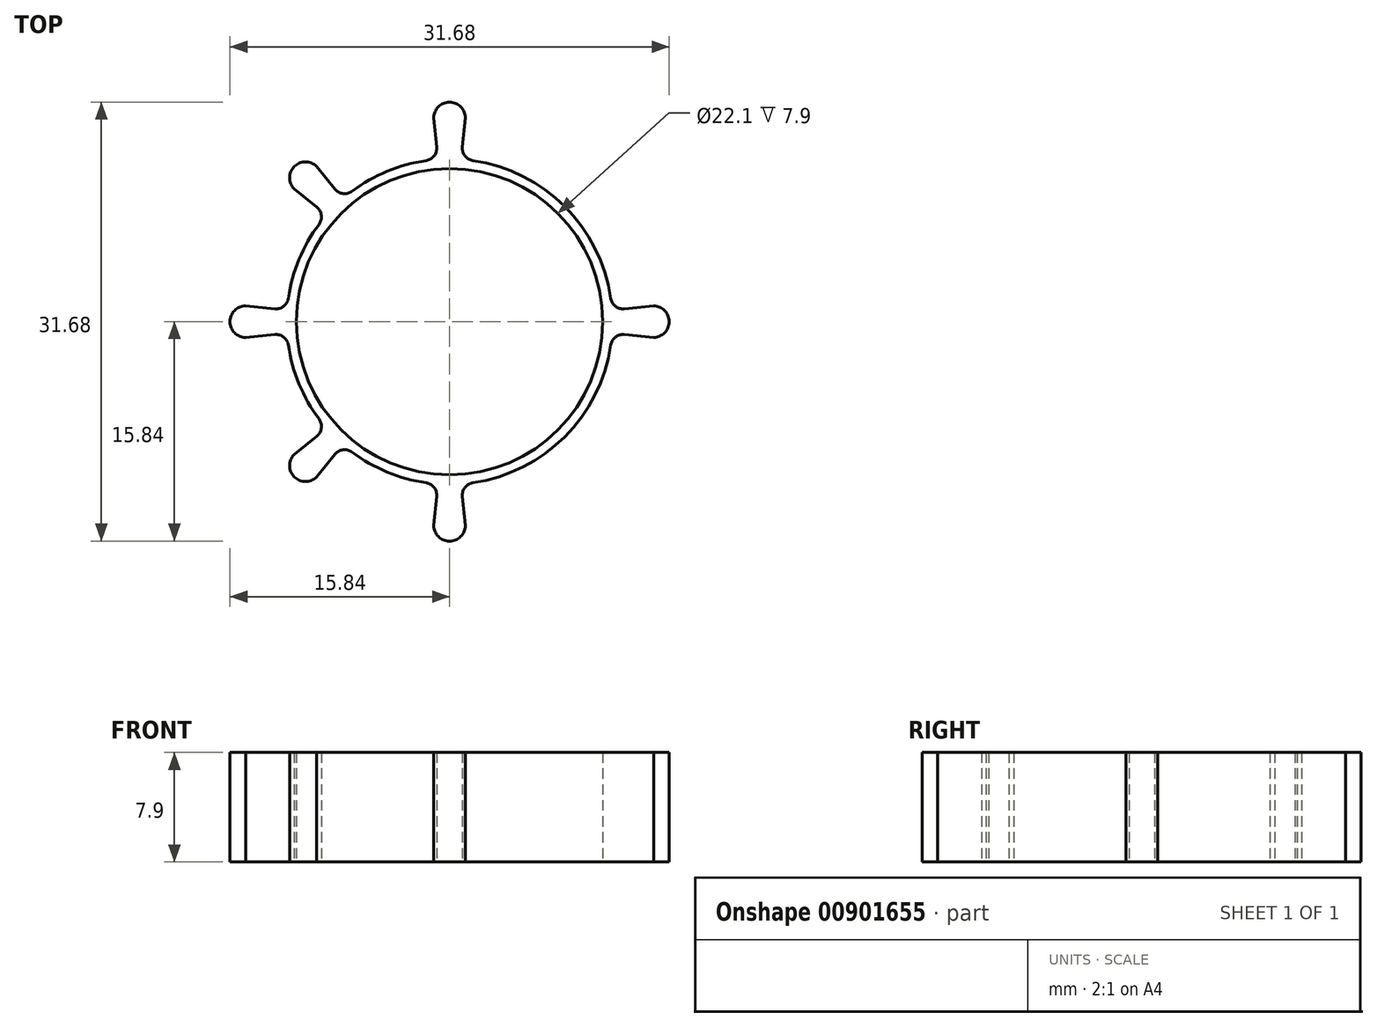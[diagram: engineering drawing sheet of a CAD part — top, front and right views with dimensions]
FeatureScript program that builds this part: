
annotation { "Feature Type Name" : "Feature", "Feature Type Description" : "" }
export const myFeature = defineFeature(function(context is Context, id is Id, definition is map)
    precondition{}
    {
        {
            var Q0;
            Q0=qCreatedBy(makeId("Top.planeOp"),FACE);
            var sketch = newSketch(context, id + "F0", { "sketchPlane" : qUnion([Q0])});
            skCircle(sketch, "E0", {"center": v(0, 0) * mm, "radius": 11.05 * mm});
            skCircle(sketch, "E1", {"center": v(0, 0) * mm, "radius": 11.75 * mm});
            skCircle(sketch, "E2", {"center": v(0, 0) * mm, "radius": 16 * mm, "construction": true});
            skLineSegment(sketch, "E3", {"start": v(-0.84, 11.72) * mm, "end": v(-1.15, 14.71) * mm});
            skLineSegment(sketch, "E4.MirrorCS", {"start": v(0.84, 11.72) * mm, "end": v(1.15, 14.71) * mm});
            skArc(sketch, "E5", {"start": v(1.15, 14.71) * mm, "mid": v(0, 15.84) * mm, "end": v(-1.15, 14.71) * mm});
            skLineSegment(sketch, "E6.MirrorCS", {"start": v(0.84, -11.72) * mm, "end": v(1.15, -14.71) * mm});
            skLineSegment(sketch, "E7.MirrorCS", {"start": v(-0.84, -11.72) * mm, "end": v(-1.15, -14.71) * mm});
            skArc(sketch, "E8.MirrorCS", {"start": v(1.15, -14.71) * mm, "mid": v(0, -15.84) * mm, "end": v(-1.15, -14.71) * mm});
            skLineSegment(sketch, "E9", {"start": v(0, 0) * mm, "end": v(-14.12, -14.12) * mm, "construction": true});
            skLineSegment(sketch, "E10", {"start": v(0, 0) * mm, "end": v(12.5, 12.5) * mm, "construction": true});
            skArc(sketch, "E11.MirrorCS", {"start": v(14.71, -1.15) * mm, "mid": v(15.84, 0) * mm, "end": v(14.71, 1.15) * mm});
            skLineSegment(sketch, "E12.MirrorCS", {"start": v(11.72, 0.84) * mm, "end": v(14.71, 1.15) * mm});
            skLineSegment(sketch, "E13.MirrorCS", {"start": v(11.72, -0.84) * mm, "end": v(14.71, -1.15) * mm});
            skLineSegment(sketch, "E14.MirrorCS", {"start": v(-11.72, 0.84) * mm, "end": v(-14.71, 1.15) * mm});
            skLineSegment(sketch, "E15.MirrorCS", {"start": v(-11.72, -0.84) * mm, "end": v(-14.71, -1.15) * mm});
            skArc(sketch, "E16.MirrorCS", {"start": v(-14.71, -1.15) * mm, "mid": v(-15.84, 0) * mm, "end": v(-14.71, 1.15) * mm});
            skLineSegment(sketch, "E17", {"start": v(0, 0) * mm, "end": v(18.87, 7.82) * mm, "construction": true});
            skLineSegment(sketch, "E18", {"start": v(0, 0) * mm, "end": v(-19, -7.87) * mm, "construction": true});
            skArc(sketch, "E19.MirrorCS", {"start": v(9.6, 11.22) * mm, "mid": v(11.2, 11.2) * mm, "end": v(11.22, 9.6) * mm});
            skLineSegment(sketch, "E20.MirrorCS", {"start": v(8.88, 7.7) * mm, "end": v(11.22, 9.6) * mm});
            skLineSegment(sketch, "E21.MirrorCS", {"start": v(7.7, 8.88) * mm, "end": v(9.6, 11.22) * mm});
            skLineSegment(sketch, "E22.MirrorCS", {"start": v(-8.88, -7.7) * mm, "end": v(-11.22, -9.6) * mm});
            skLineSegment(sketch, "E23.MirrorCS", {"start": v(-7.7, -8.88) * mm, "end": v(-9.6, -11.22) * mm});
            skArc(sketch, "E24.MirrorCS", {"start": v(-11.22, -9.6) * mm, "mid": v(-11.2, -11.2) * mm, "end": v(-9.6, -11.22) * mm});
            skLineSegment(sketch, "E25", {"start": v(0, 0) * mm, "end": v(-24.8, 10.27) * mm, "construction": true});
            skLineSegment(sketch, "E26", {"start": v(0, 0) * mm, "end": v(24.1, -9.98) * mm, "construction": true});
            skArc(sketch, "E27.MirrorCS", {"start": v(11.22, -9.6) * mm, "mid": v(11.2, -11.2) * mm, "end": v(9.6, -11.22) * mm});
            skLineSegment(sketch, "E28.MirrorCS", {"start": v(7.7, -8.88) * mm, "end": v(9.6, -11.22) * mm});
            skLineSegment(sketch, "E29.MirrorCS", {"start": v(8.88, -7.7) * mm, "end": v(11.22, -9.6) * mm});
            skLineSegment(sketch, "E30.MirrorCS", {"start": v(-7.7, 8.88) * mm, "end": v(-9.6, 11.22) * mm});
            skLineSegment(sketch, "E31.MirrorCS", {"start": v(-8.88, 7.7) * mm, "end": v(-11.22, 9.6) * mm});
            skArc(sketch, "E32.MirrorCS", {"start": v(-9.6, 11.22) * mm, "mid": v(-11.2, 11.2) * mm, "end": v(-11.22, 9.6) * mm});
            skSolve(sketch);
        }
        {
            var Q0;
            {var subQ0=sQuery(id+"F0.wireOp",EDGE,"E30.MirrorCS");Q0=makeQuery(id+"F0.imprint","IMPRINT",FACE,{"disambiguationData":[TD([[makeQuery(id+"F0.imprint","IMPRINT",EDGE,{"derivedFrom":subQ0}),1.0]])]});}
            var Q1;
            Q1=makeQuery(id+"F0.imprint","IMPRINT",FACE,{"disambiguationData":[TD([[makeQuery(id+"F0.imprint","IMPRINT",EDGE,{"derivedFrom":sQuery(id+"F0.wireOp",EDGE,"E0")}),-1.0]])]});
            var Q2;
            {var subQ0=sQuery(id+"F0.wireOp",EDGE,"E3");Q2=makeQuery(id+"F0.imprint","IMPRINT",FACE,{"disambiguationData":[TD([[makeQuery(id+"F0.imprint","IMPRINT",EDGE,{"derivedFrom":subQ0}),-1.0]])]});}
            var Q3;
            Q3=makeQuery(id+"F0.imprint","IMPRINT",FACE,{"disambiguationData":[TD([[makeQuery(id+"F0.imprint","IMPRINT",EDGE,{"derivedFrom":sQuery(id+"F0.wireOp",EDGE,"E19.MirrorCS")}),-1.0]])]});
            var Q4;
            Q4=makeQuery(id+"F0.imprint","IMPRINT",FACE,{"disambiguationData":[TD([[makeQuery(id+"F0.imprint","IMPRINT",EDGE,{"derivedFrom":sQuery(id+"F0.wireOp",EDGE,"E11.MirrorCS")}),1.0]])]});
            var Q5;
            Q5=makeQuery(id+"F0.imprint","IMPRINT",FACE,{"disambiguationData":[TD([[makeQuery(id+"F0.imprint","IMPRINT",EDGE,{"derivedFrom":sQuery(id+"F0.wireOp",EDGE,"E27.MirrorCS")}),-1.0]])]});
            var Q6;
            {var subQ0=sQuery(id+"F0.wireOp",EDGE,"E6.MirrorCS");Q6=makeQuery(id+"F0.imprint","IMPRINT",FACE,{"disambiguationData":[TD([[makeQuery(id+"F0.imprint","IMPRINT",EDGE,{"derivedFrom":subQ0}),-1.0]])]});}
            var Q7;
            {var subQ0=sQuery(id+"F0.wireOp",EDGE,"E22.MirrorCS");Q7=makeQuery(id+"F0.imprint","IMPRINT",FACE,{"disambiguationData":[TD([[makeQuery(id+"F0.imprint","IMPRINT",EDGE,{"derivedFrom":subQ0}),1.0]])]});}
            var Q8;
            {var subQ0=sQuery(id+"F0.wireOp",EDGE,"E14.MirrorCS");Q8=makeQuery(id+"F0.imprint","IMPRINT",FACE,{"disambiguationData":[TD([[makeQuery(id+"F0.imprint","IMPRINT",EDGE,{"derivedFrom":subQ0}),1.0]])]});}
            extrude(context, id + "F1", {"entities" : qUnion([Q0, Q1, Q2, Q3, Q4, Q5, Q6, Q7, Q8]), "depth" : 7.9 * mm, "offsetDistance" : 25.4 * mm});
        }
        {
            var Q0;
            Q0=makeQuery(id+"F1.opExtrude","SWEPT_EDGE",EDGE,{"disambiguationData":[OSD([sQuery(id+"F0.wireOp",EDGE,"E1"),sQuery(id+"F0.wireOp",EDGE,"E22.MirrorCS")])]});
            var Q1;
            Q1=makeQuery(id+"F1.opExtrude","SWEPT_EDGE",EDGE,{"disambiguationData":[OSD([sQuery(id+"F0.wireOp",EDGE,"E1"),sQuery(id+"F0.wireOp",EDGE,"E15.MirrorCS")])]});
            var Q2;
            Q2=makeQuery(id+"F1.opExtrude","SWEPT_EDGE",EDGE,{"disambiguationData":[OSD([sQuery(id+"F0.wireOp",EDGE,"E1"),sQuery(id+"F0.wireOp",EDGE,"E23.MirrorCS")])]});
            var Q3;
            Q3=makeQuery(id+"F1.opExtrude","SWEPT_EDGE",EDGE,{"disambiguationData":[OSD([sQuery(id+"F0.wireOp",EDGE,"E1"),sQuery(id+"F0.wireOp",EDGE,"E7.MirrorCS")])]});
            var Q4;
            Q4=makeQuery(id+"F1.opExtrude","SWEPT_EDGE",EDGE,{"disambiguationData":[OSD([sQuery(id+"F0.wireOp",EDGE,"E1"),sQuery(id+"F0.wireOp",EDGE,"E28.MirrorCS")])]});
            var Q5;
            Q5=makeQuery(id+"F1.opExtrude","SWEPT_EDGE",EDGE,{"disambiguationData":[OSD([sQuery(id+"F0.wireOp",EDGE,"E1"),sQuery(id+"F0.wireOp",EDGE,"E6.MirrorCS")])]});
            var Q6;
            Q6=makeQuery(id+"F1.opExtrude","SWEPT_EDGE",EDGE,{"disambiguationData":[OSD([sQuery(id+"F0.wireOp",EDGE,"E1"),sQuery(id+"F0.wireOp",EDGE,"E29.MirrorCS")])]});
            var Q7;
            Q7=makeQuery(id+"F1.opExtrude","SWEPT_EDGE",EDGE,{"disambiguationData":[OSD([sQuery(id+"F0.wireOp",EDGE,"E1"),sQuery(id+"F0.wireOp",EDGE,"E13.MirrorCS")])]});
            var Q8;
            Q8=makeQuery(id+"F1.opExtrude","SWEPT_EDGE",EDGE,{"disambiguationData":[OSD([sQuery(id+"F0.wireOp",EDGE,"E1"),sQuery(id+"F0.wireOp",EDGE,"E12.MirrorCS")])]});
            var Q9;
            Q9=makeQuery(id+"F1.opExtrude","SWEPT_EDGE",EDGE,{"disambiguationData":[OSD([sQuery(id+"F0.wireOp",EDGE,"E1"),sQuery(id+"F0.wireOp",EDGE,"E20.MirrorCS")])]});
            var Q10;
            Q10=makeQuery(id+"F1.opExtrude","SWEPT_EDGE",EDGE,{"disambiguationData":[OSD([sQuery(id+"F0.wireOp",EDGE,"E1"),sQuery(id+"F0.wireOp",EDGE,"E4.MirrorCS")])]});
            var Q11;
            Q11=makeQuery(id+"F1.opExtrude","SWEPT_EDGE",EDGE,{"disambiguationData":[OSD([sQuery(id+"F0.wireOp",EDGE,"E1"),sQuery(id+"F0.wireOp",EDGE,"E21.MirrorCS")])]});
            var Q12;
            Q12=makeQuery(id+"F1.opExtrude","SWEPT_EDGE",EDGE,{"disambiguationData":[OSD([sQuery(id+"F0.wireOp",EDGE,"E1"),sQuery(id+"F0.wireOp",EDGE,"E3")])]});
            var Q13;
            Q13=makeQuery(id+"F1.opExtrude","SWEPT_EDGE",EDGE,{"disambiguationData":[OSD([sQuery(id+"F0.wireOp",EDGE,"E1"),sQuery(id+"F0.wireOp",EDGE,"E30.MirrorCS")])]});
            var Q14;
            Q14=makeQuery(id+"F1.opExtrude","SWEPT_EDGE",EDGE,{"disambiguationData":[OSD([sQuery(id+"F0.wireOp",EDGE,"E1"),sQuery(id+"F0.wireOp",EDGE,"E31.MirrorCS")])]});
            var Q15;
            Q15=makeQuery(id+"F1.opExtrude","SWEPT_EDGE",EDGE,{"disambiguationData":[OSD([sQuery(id+"F0.wireOp",EDGE,"E1"),sQuery(id+"F0.wireOp",EDGE,"E14.MirrorCS")])]});
            fillet(context, id + "F2", {"entities" : qUnion([Q0, Q1, Q2, Q3, Q4, Q5, Q6, Q7, Q8, Q9, Q10, Q11, Q12, Q13, Q14, Q15]), "radius" : 0.89 * mm, "tangentPropagation" : true, "allowEdgeOverflow" : false});
        }
    });
